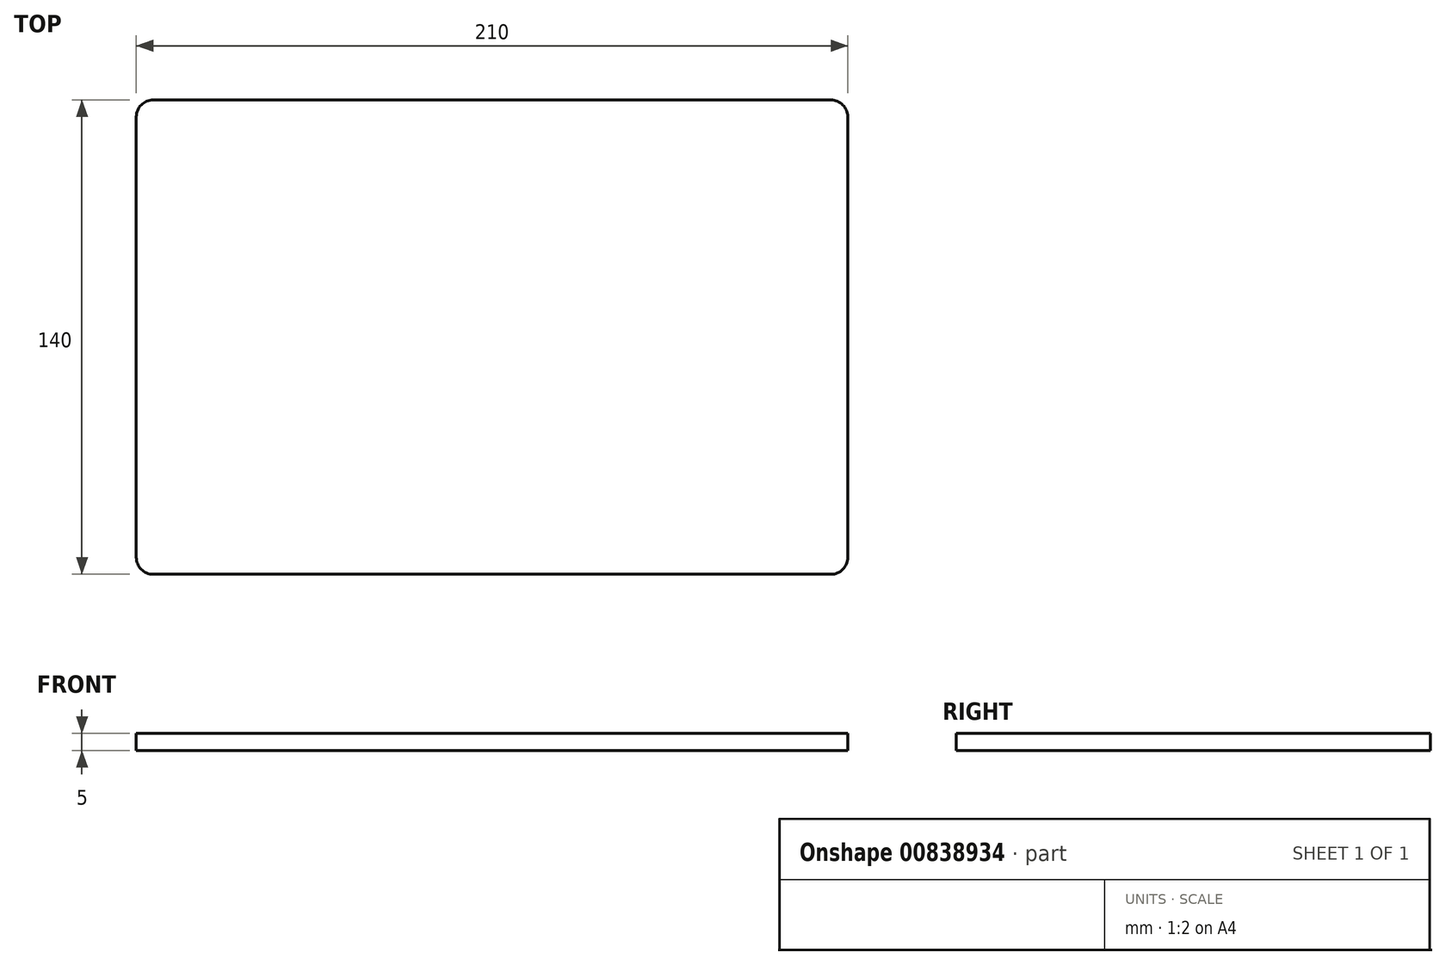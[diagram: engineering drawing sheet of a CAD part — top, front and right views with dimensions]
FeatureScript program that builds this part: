
annotation { "Feature Type Name" : "Feature", "Feature Type Description" : "" }
export const myFeature = defineFeature(function(context is Context, id is Id, definition is map)
    precondition{}
    {
        {
            var Q0;
            Q0=qCreatedBy(makeId("Top.planeOp"),FACE);
            var sketch = newSketch(context, id + "F0", { "sketchPlane" : qUnion([Q0])});
            skLineSegment(sketch, "E0.bottom", {"start": v(100, -70) * mm, "end": v(-100, -70) * mm});
            skLineSegment(sketch, "E0.top", {"start": v(100, 70) * mm, "end": v(-100, 70) * mm});
            skLineSegment(sketch, "E0.left", {"start": v(105, -65) * mm, "end": v(105, 65) * mm});
            skLineSegment(sketch, "E0.right", {"start": v(-105, -65) * mm, "end": v(-105, 65) * mm});
            skPoint(sketch, "E0.middle", {"position": v(0, 0) * mm});
            skPoint(sketch, "E1.visualSharp", {"position": v(-105, 70) * mm});
            skArc(sketch, "E1.filletArc", {"start": v(-100, 70) * mm, "mid": v(-103.54, 68.54) * mm, "end": v(-105, 65) * mm});
            skPoint(sketch, "E2.visualSharp", {"position": v(105, 70) * mm});
            skArc(sketch, "E2.filletArc", {"start": v(105, 65) * mm, "mid": v(103.54, 68.54) * mm, "end": v(100, 70) * mm});
            skPoint(sketch, "E3.visualSharp", {"position": v(105, -70) * mm});
            skArc(sketch, "E3.filletArc", {"start": v(100, -70) * mm, "mid": v(103.54, -68.54) * mm, "end": v(105, -65) * mm});
            skPoint(sketch, "E4.visualSharp", {"position": v(-105, -70) * mm});
            skArc(sketch, "E4.filletArc", {"start": v(-105, -65) * mm, "mid": v(-103.54, -68.54) * mm, "end": v(-100, -70) * mm});
            skSolve(sketch);
        }
        {
            var Q0;
            Q0=makeQuery(id+"F0.imprint","IMPRINT",FACE,{"disambiguationData":[TD([[makeQuery(id+"F0.imprint","IMPRINT",EDGE,{"derivedFrom":sQuery(id+"F0.wireOp",EDGE,"E0.bottom")}),-1.0]])]});
            extrude(context, id + "F1", {"entities" : qUnion([Q0]), "depth" : 5 * mm, "offsetDistance" : 25 * mm});
        }
    });
